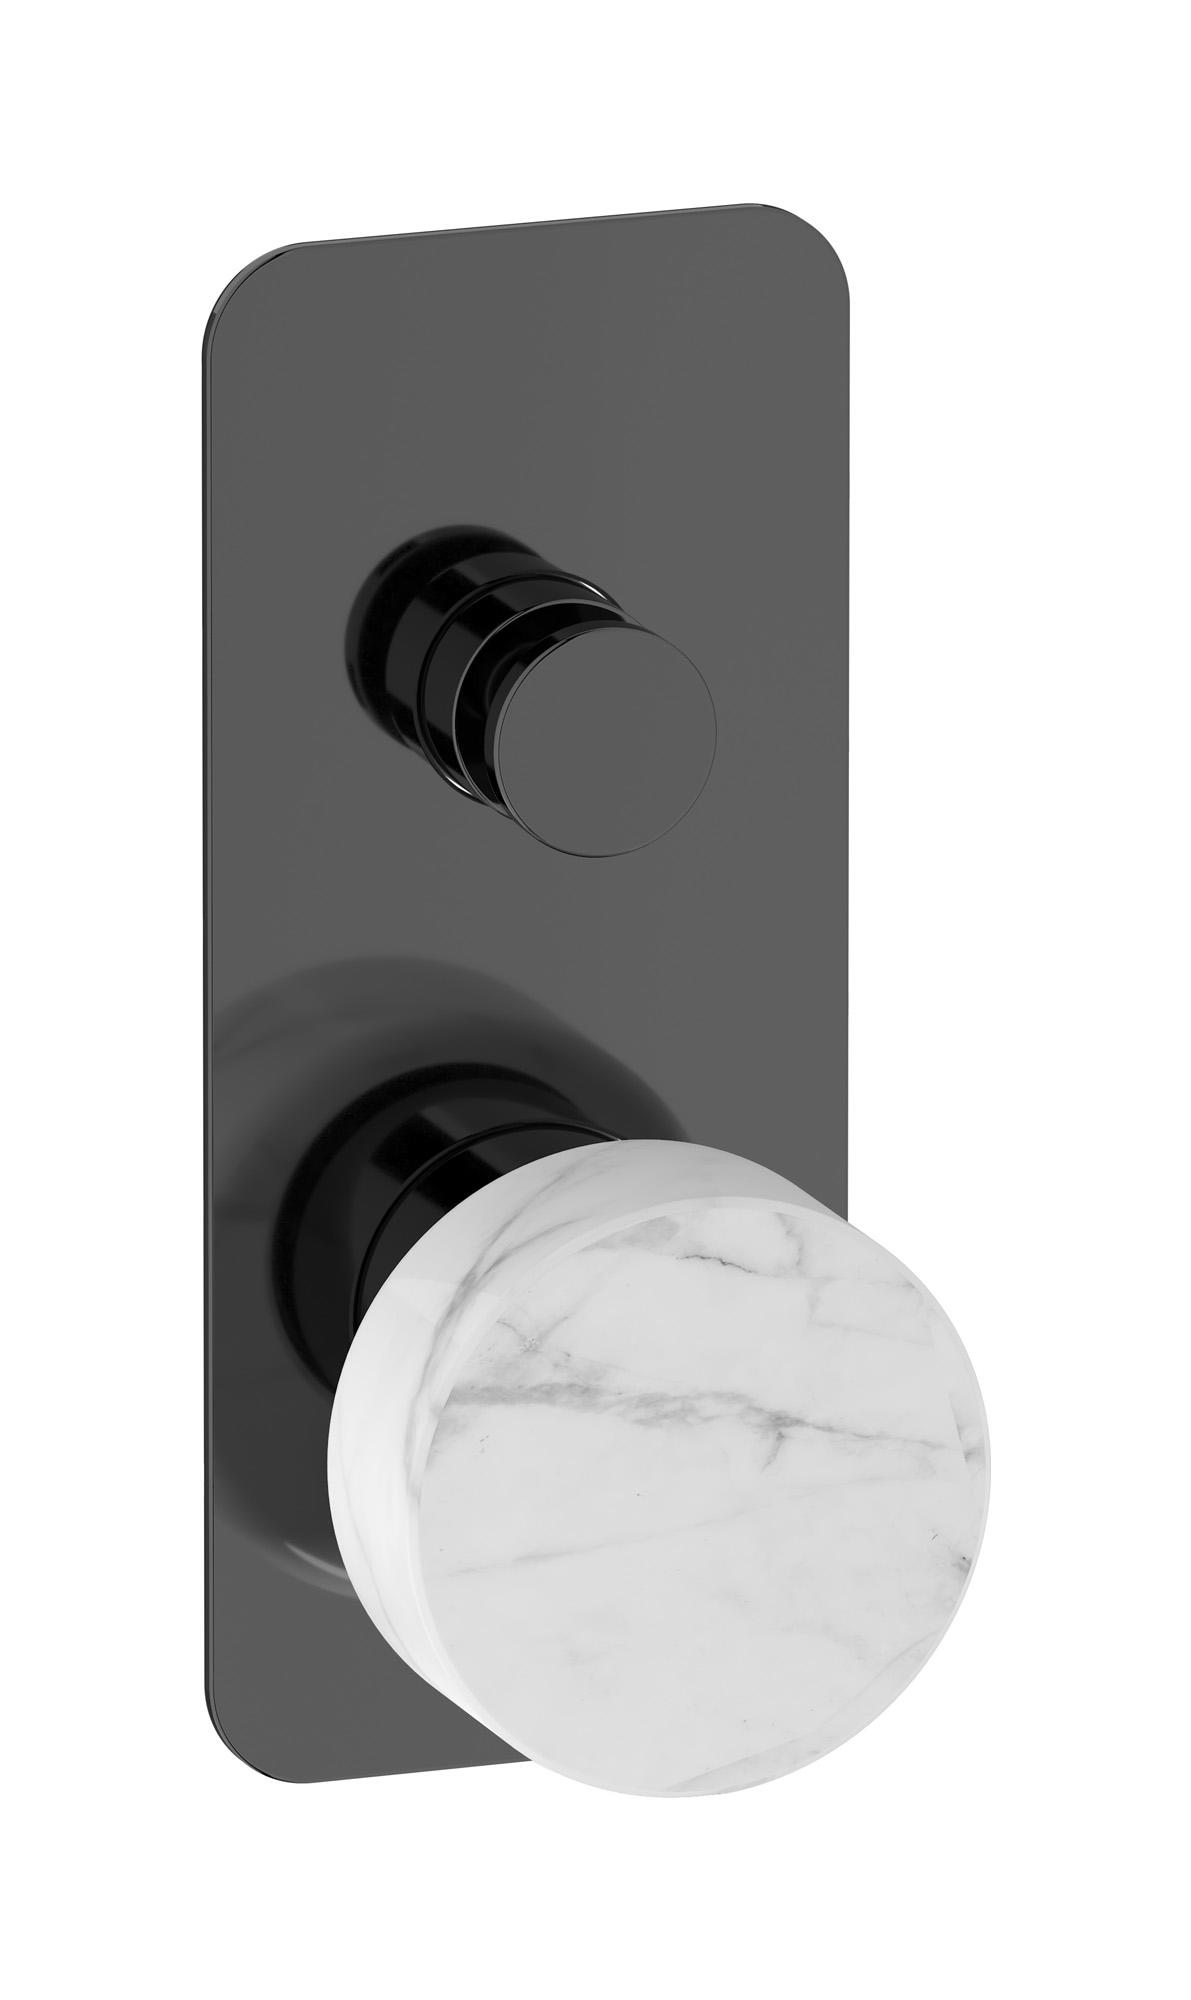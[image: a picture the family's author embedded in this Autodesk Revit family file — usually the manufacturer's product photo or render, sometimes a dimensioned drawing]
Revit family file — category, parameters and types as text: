
# Revit family: MR310_1
name_source: partatom
category: Apparecchi idraulici
units: mm (PartAtom-declared; Revit-internal decimal feet)

## family parameters
Basato su piano di lavoro = No
Condiviso = No
Mantieni orientamento annotazione = No
Numero OmniClass = 23.45.55.17
Punto di calcolo locali = No
Quota connettore circolare = Usa diametro
Sempre verticale = Sì
Taglio con vuoti quando caricato = No
Tipo di parte = Normale
Titolo OmniClass = Mixing Faucets

## types (14) — shared parameters
Cold water inlet = 10 mm  [stored 0.0328084 ft]
Commenti sul tipo = Wall mixer
Connessione CW = No
Connessione HW = No
Connessione di scarico = No
Connessione di ventilazione = No
Descrizione = Exposed parts for manual wall mixer with two ways diverter
Hot water inlet = 10 mm  [stored 0.0328084 ft]
Produttore = IB Rubinetterie S.p.A.
URL = https://www.weareib.it
zero-valued in all types: Prospetto di default

## per-type parameters (varying)
| type | Finishes surface | Immagine tipo | Modello |
| Chrome | IB_Chrome | MR310CC_1.jpg | MR310CC_1 |
| Platinum | IB_Platinum | MR310PL_1.jpg | MR310PL_1 |
| Brushed nickel | IB_Brushed nickel | MR310SS_1.jpg | MR310SS_1 |
| Natural brass | IB_Brass | MR310ON_1.jpg | MR310ON_1 |
| Matt white | IB_matt white | MR310BO_1.jpg | MR310BO_1 |
| Matt black | IB_matt black | MR310NP_1.jpg | MR310NP_1 |
| Black chrome | IB_Black chrome | MR310CF_1.jpg | MR310CF_1 |
| Brushed black chrome | IB_Brushed black chrome | MR310CS_1.jpg | MR310CS_1 |
| Pale gold | IB_Pale gold | MR310II_1.jpg | MR310II_1 |
| Brushed pale gold | IB_brushed pale gold | MR310IS_1.jpg | MR310IS_1 |
| Rose gold | IB_Rose gold | MR310RS_1.jpg | MR310RS_1 |
| Brushed rose gold | IB_Brushed rose gold | MR310SR_1.jpg | MR310SR_1 |
| Gold | IB_gold | MR310OO_1.jpg | MR310OO_1 |
| Brushed gold | IB_brushed gold | MR310OS_1.jpg | MR310OS_1 |

note: [stored X ft] marks values corroborated as IEEE doubles in the binary element streams (Revit-internal decimal feet)
